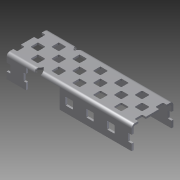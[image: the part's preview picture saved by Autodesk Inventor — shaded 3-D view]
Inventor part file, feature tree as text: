
AUTODESK INVENTOR PART (.ipt)
format: ipt  version: 2012 (Build 160160000, 160)  size: 890,880 bytes
history: native  units: in
note: dims shown in document units (in); Inventor stores cm internally (conversion verified against a paired STEP export)
features: other x2, plane x2, split x2, imported_body x1, extrude x1, sketch x1
ambient origin geometry x8: Origin, YZ Plane, XZ Plane, XY Plane, X Axis, Y Axis, Z Axis, Center Point
feature tree (9):
  parser-record x1  (decoder bookkeeping rows leaked as tree rows — omitted from the tree; the rows remain in map.json)
  imported_body  "Base1"
  plane  "Work Plane1"
  split  "Split1"
  plane  "Work Plane2"
  split  "Split2"
  extrude  "Extrusion1"  [1 undecoded]
  other  "Alias Freeform1"
  sketch  "Sketch1"  dims[d0=-0.25in d1=-1.75in d2=1.0in d3=0.0in]
note: 1 required parameter value undecoded (feature->parameter linkage not recoverable at this tier; creation-order binding heuristic only, values carry confidence <= 0.55)
